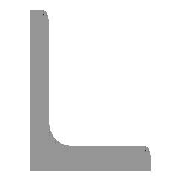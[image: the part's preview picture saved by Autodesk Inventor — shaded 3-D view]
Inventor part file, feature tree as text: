
AUTODESK INVENTOR PART (.ipt)
format: ipt  version: 2021 (Build 250183000, 183)  size: 116,736 bytes
history: native  units: mm (DEFAULTED — no unit token found)
features: other x3, sketch x2, extrude x1, plane x1
ambient origin geometry x8: Origin, YZ Plane, XZ Plane, XY Plane, X Axis, Y Axis, Z Axis, Center Point
bodies: Solid1 (feature_tree)
feature tree (7):
  other  "Driven Length"
  other  "Płaszczyzna początkowa"
  other  "Płaszczyzna końcowa"
  extrude  "Bryła"  Depth=25.0mm
  sketch  "Sketch3"  dims[d0=25.0mm d1=25.0mm]
  plane  "Work Plane3"
  sketch  "Sketch4"  dims[d2=3.0mm d3=3.0mm d4=200.0mm d5=0.0mm d8=4.5mm d9=3.0mm d10=0.0mm d11=0.0mm d12=-0.0mm d13=200.0mm d14=90.0deg d15=200.0mm]
